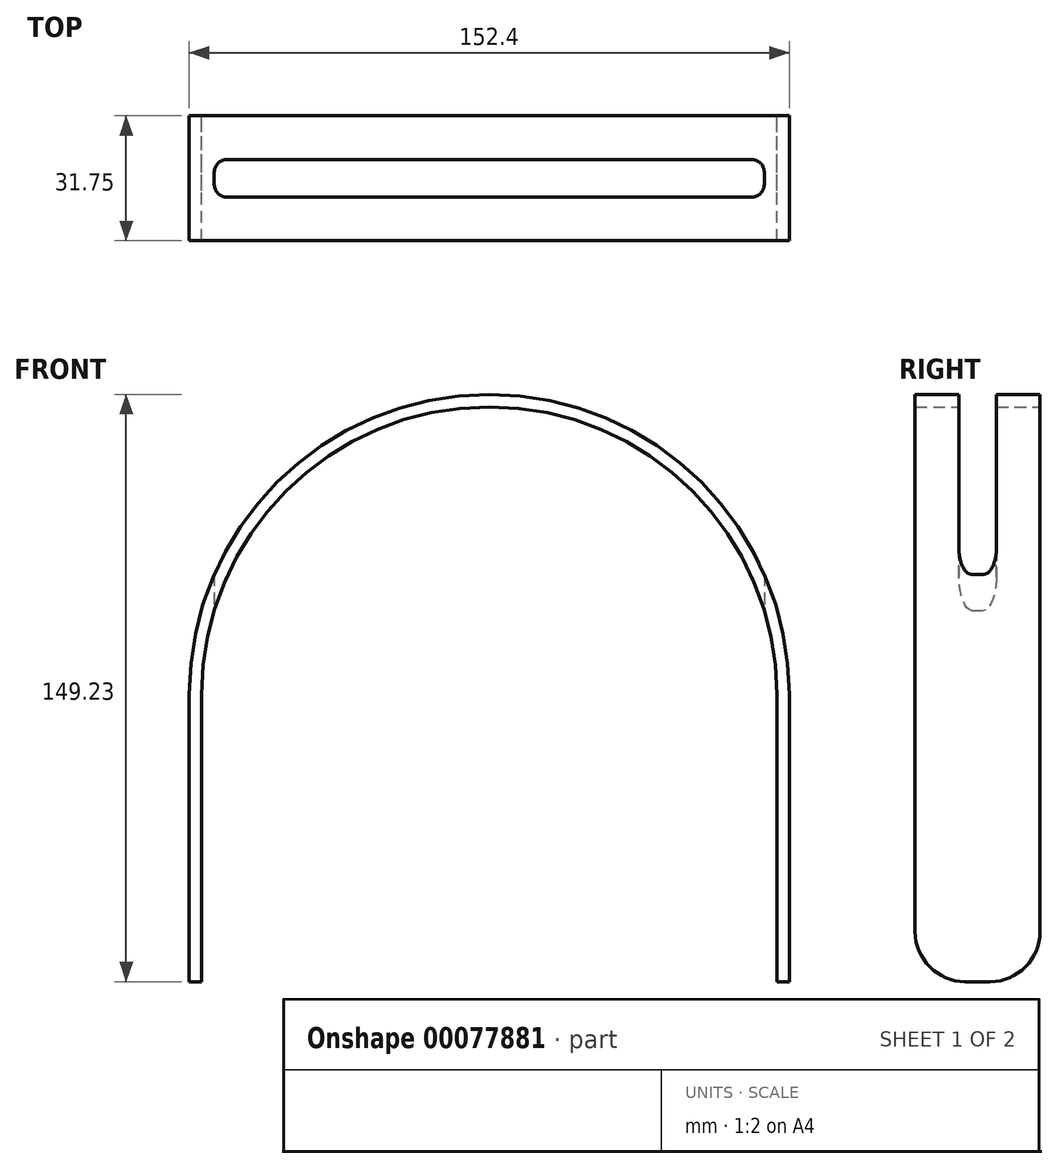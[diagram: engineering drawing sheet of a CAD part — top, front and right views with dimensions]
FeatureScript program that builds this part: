
annotation { "Feature Type Name" : "Feature", "Feature Type Description" : "" }
export const myFeature = defineFeature(function(context is Context, id is Id, definition is map)
    precondition{}
    {
        {
            var Q0;
            Q0=qCreatedBy(makeId("Front.planeOp"),FACE);
            var sketch = newSketch(context, id + "F0", { "sketchPlane" : qUnion([Q0])});
            skArc(sketch, "E0", {"start": v(73.03, 0) * mm, "mid": v(0, 73.03) * mm, "end": v(-73.03, 0) * mm});
            skLineSegment(sketch, "E1", {"start": v(-73.03, 0) * mm, "end": v(-73.03, -73.03) * mm});
            skLineSegment(sketch, "E2", {"start": v(0, 0) * mm, "end": v(0, 109.65) * mm, "construction": true});
            skLineSegment(sketch, "E3.MirrorCS", {"start": v(73.03, 0) * mm, "end": v(73.03, -73.03) * mm});
            skLineSegment(sketch, "E4.0", {"start": v(-76.2, 0) * mm, "end": v(-76.2, -73.03) * mm});
            skArc(sketch, "E4.1", {"start": v(76.2, 0) * mm, "mid": v(0, 76.2) * mm, "end": v(-76.2, 0) * mm});
            skLineSegment(sketch, "E4.2", {"start": v(76.2, 0) * mm, "end": v(76.2, -73.03) * mm});
            skLineSegment(sketch, "E5", {"start": v(-76.2, -73.03) * mm, "end": v(-73.03, -73.03) * mm});
            skLineSegment(sketch, "E6", {"start": v(73.03, -73.03) * mm, "end": v(76.2, -73.03) * mm});
            skSolve(sketch);
        }
        {
            var Q0;
            Q0=makeQuery(id+"F0.imprint","IMPRINT",FACE,{"disambiguationData":[TD([[makeQuery(id+"F0.imprint","IMPRINT",EDGE,{"derivedFrom":sQuery(id+"F0.wireOp",EDGE,"E0")}),-1.0]])]});
            extrude(context, id + "F1", {"entities" : qUnion([Q0]), "depth" : 31.75 * mm});
        }
        {
            var Q0;
            Q0=makeQuery(id+"F1.opExtrude","CAP_EDGE",EDGE,{"disambiguationData":[OSD([sQuery(id+"F0.wireOp",EDGE,"E5")])],"isStart":false});
            var Q1;
            Q1=makeQuery(id+"F1.opExtrude","CAP_EDGE",EDGE,{"disambiguationData":[OSD([sQuery(id+"F0.wireOp",EDGE,"E5")])],"isStart":true});
            var Q2;
            Q2=makeQuery(id+"F1.opExtrude","CAP_EDGE",EDGE,{"disambiguationData":[OSD([sQuery(id+"F0.wireOp",EDGE,"E6")])],"isStart":false});
            var Q3;
            Q3=makeQuery(id+"F1.opExtrude","CAP_EDGE",EDGE,{"disambiguationData":[OSD([sQuery(id+"F0.wireOp",EDGE,"E6")])],"isStart":true});
            fillet(context, id + "F2", {"entities" : qUnion([Q0, Q1, Q2, Q3]), "radius" : 12.7 * mm, "tangentPropagation" : true, "allowEdgeOverflow" : false});
        }
        {
            var Q0;
            Q0=qCreatedBy(makeId("Top.planeOp"),FACE);
            var sketch = newSketch(context, id + "F3", { "sketchPlane" : qUnion([Q0])});
            skLineSegment(sketch, "E7.0", {"start": v(76.2, -31.75) * mm, "end": v(-76.2, -31.75) * mm, "construction": true});
            skLineSegment(sketch, "E7.1", {"start": v(76.2, 0) * mm, "end": v(-76.2, 0) * mm, "construction": true});
            skLineSegment(sketch, "E8", {"start": v(0, -31.75) * mm, "end": v(0, 0) * mm, "construction": true});
            skLineSegment(sketch, "E9.bottom", {"start": v(-66.68, -20.64) * mm, "end": v(66.68, -20.64) * mm});
            skLineSegment(sketch, "E9.top", {"start": v(-66.68, -11.11) * mm, "end": v(66.68, -11.11) * mm});
            skLineSegment(sketch, "E9.left", {"start": v(-69.85, -17.46) * mm, "end": v(-69.85, -14.29) * mm});
            skLineSegment(sketch, "E9.right", {"start": v(69.85, -17.46) * mm, "end": v(69.85, -14.29) * mm});
            skPoint(sketch, "E9.middle", {"position": v(0, -15.88) * mm});
            skPoint(sketch, "E10.visualSharp", {"position": v(69.85, -20.64) * mm});
            skArc(sketch, "E10.filletArc", {"start": v(66.68, -20.64) * mm, "mid": v(68.92, -19.7) * mm, "end": v(69.85, -17.46) * mm});
            skPoint(sketch, "E11.visualSharp", {"position": v(69.85, -11.11) * mm});
            skArc(sketch, "E11.filletArc", {"start": v(69.85, -14.29) * mm, "mid": v(68.92, -12.04) * mm, "end": v(66.68, -11.11) * mm});
            skPoint(sketch, "E12.visualSharp", {"position": v(-69.85, -11.11) * mm});
            skArc(sketch, "E12.filletArc", {"start": v(-66.68, -11.11) * mm, "mid": v(-68.92, -12.04) * mm, "end": v(-69.85, -14.29) * mm});
            skPoint(sketch, "E13.visualSharp", {"position": v(-69.85, -20.64) * mm});
            skArc(sketch, "E13.filletArc", {"start": v(-69.85, -17.46) * mm, "mid": v(-68.92, -19.7) * mm, "end": v(-66.68, -20.64) * mm});
            skSolve(sketch);
        }
        {
            var Q0;
            Q0=makeQuery(id+"F3.imprint","IMPRINT",FACE,{"disambiguationData":[TD([[makeQuery(id+"F3.imprint","IMPRINT",EDGE,{"derivedFrom":sQuery(id+"F3.wireOp",EDGE,"E9.bottom")}),1.0]])]});
            extrude(context, id + "F4", {"entities" : qUnion([Q0]), "operationType" : NewBodyOperationType.REMOVE, "endBound" : BoundingType.THROUGH_ALL, "depth" : 25.4 * mm});
        }
    });
